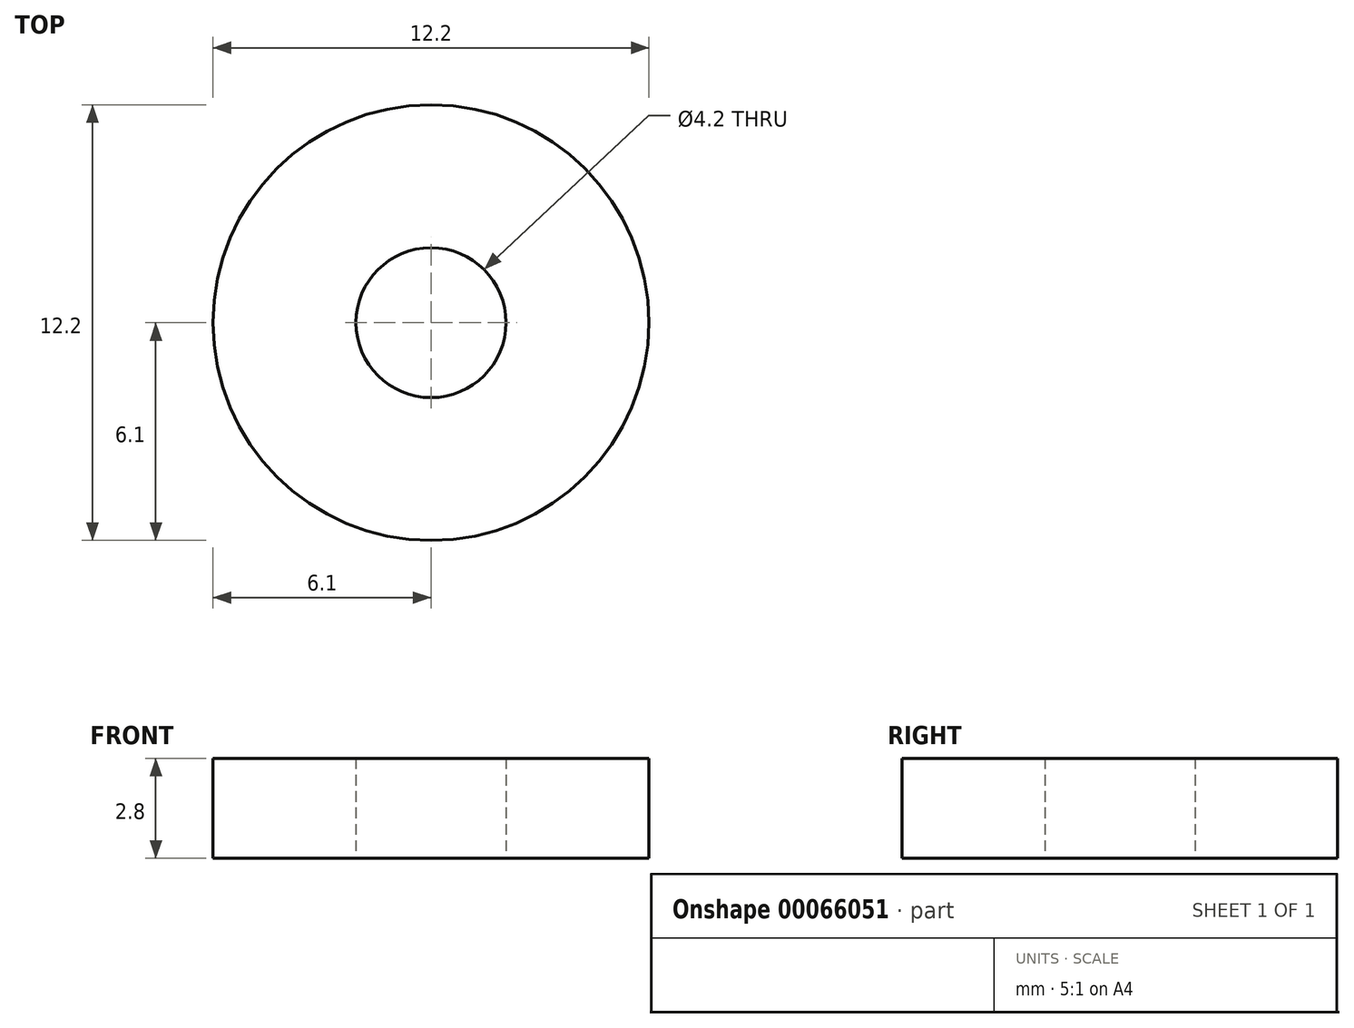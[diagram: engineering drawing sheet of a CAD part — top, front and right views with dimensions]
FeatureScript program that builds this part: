
annotation { "Feature Type Name" : "Feature", "Feature Type Description" : "" }
export const myFeature = defineFeature(function(context is Context, id is Id, definition is map)
    precondition{}
    {
        {
            var Q0;
            Q0=qCreatedBy(makeId("Top.planeOp"),FACE);
            var sketch = newSketch(context, id + "F0", { "sketchPlane" : qUnion([Q0])});
            skCircle(sketch, "E0", {"center": v(0, 0) * mm, "radius": 2.1 * mm});
            skCircle(sketch, "E1", {"center": v(0, 0) * mm, "radius": 6.1 * mm});
            skSolve(sketch);
        }
        {
            var Q0;
            Q0=makeQuery(id+"F0.imprint","IMPRINT",FACE,{"disambiguationData":[TD([[makeQuery(id+"F0.imprint","IMPRINT",EDGE,{"derivedFrom":sQuery(id+"F0.wireOp",EDGE,"E0")}),-1.0]])]});
            extrude(context, id + "F1", {"entities" : qUnion([Q0]), "flatOperationType" : FlatOperationType.REMOVE, "offsetDistance" : 25 * mm, "depth" : (5.6 / 2) * mm, "domain" : OperationDomain.MODEL});
        }
    });
